# Revit family: rba-bim-rba4601-18 Series
name_source: partatom
category: Plumbing Fixtures
revit_build: Autodesk Revit 2016 (Build: 20151007_0715(x64)
units: mm (PartAtom-declared; Revit-internal decimal feet)

## family parameters
Always vertical = Yes
Cut with Voids When Loaded = No
Part Type = Normal
Room Calculation Point = No
Round Connector Dimension = Use Diameter
Shared = No
Work Plane-Based = No

## types (3) — shared parameters
Description = 90° WC Rail, Right Hand
Manufacturer = RBA Group
Manufacturer Model = -
Modified Issue = 20180918.01
URL = http://www.rba.com.au

## per-type parameters (varying)
| type | Materials and Finishes |
| RBA4601-181 | Stainless Steel / White Antibacterial Finish |
| RBA4601-188 | Stainless Steel / Matte Black Antibacterial Finish |
| RBA4601-189 | Stainless Steel / Chrome |

note: column(s) folded — value = type name in every type: Model

## geometry (parser evidence)
native form markers: Blend x18, Sweep x4
no freeform markers — native parametric forms only
